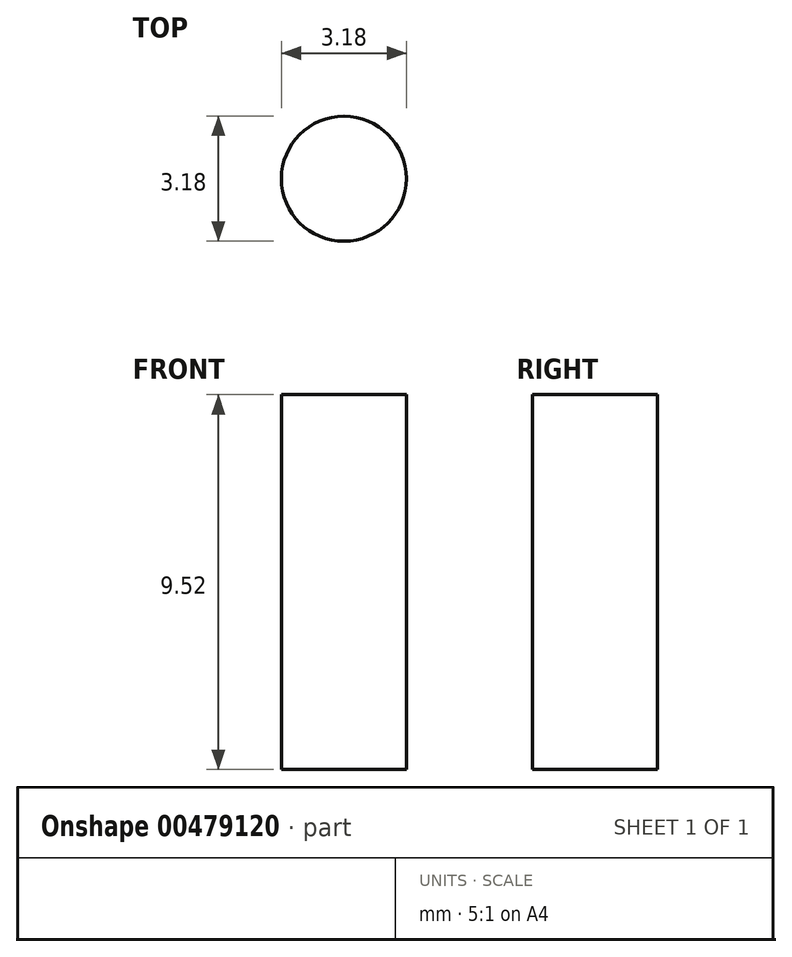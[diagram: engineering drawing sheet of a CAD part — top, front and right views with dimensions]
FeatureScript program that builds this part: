
annotation { "Feature Type Name" : "Feature", "Feature Type Description" : "" }
export const myFeature = defineFeature(function(context is Context, id is Id, definition is map)
    precondition{}
    {
        {
            var Q0;
            Q0=qCreatedBy(makeId("Top.planeOp"),FACE);
            var sketch = newSketch(context, id + "F0", { "sketchPlane" : qUnion([Q0])});
            skCircle(sketch, "E0", {"center": v(0, 0) * mm, "radius": 1.59 * mm});
            skSolve(sketch);
        }
        {
            var Q0;
            Q0=makeQuery(id+"F0.imprint","IMPRINT",FACE,{"disambiguationData":[TD([[makeQuery(id+"F0.imprint","IMPRINT",EDGE,{"derivedFrom":sQuery(id+"F0.wireOp",EDGE,"E0")}),1.0]])]});
            extrude(context, id + "F1", {"entities" : qUnion([Q0]), "endBound" : BoundingType.SYMMETRIC, "depth" : 9.52 * mm});
        }
    });
